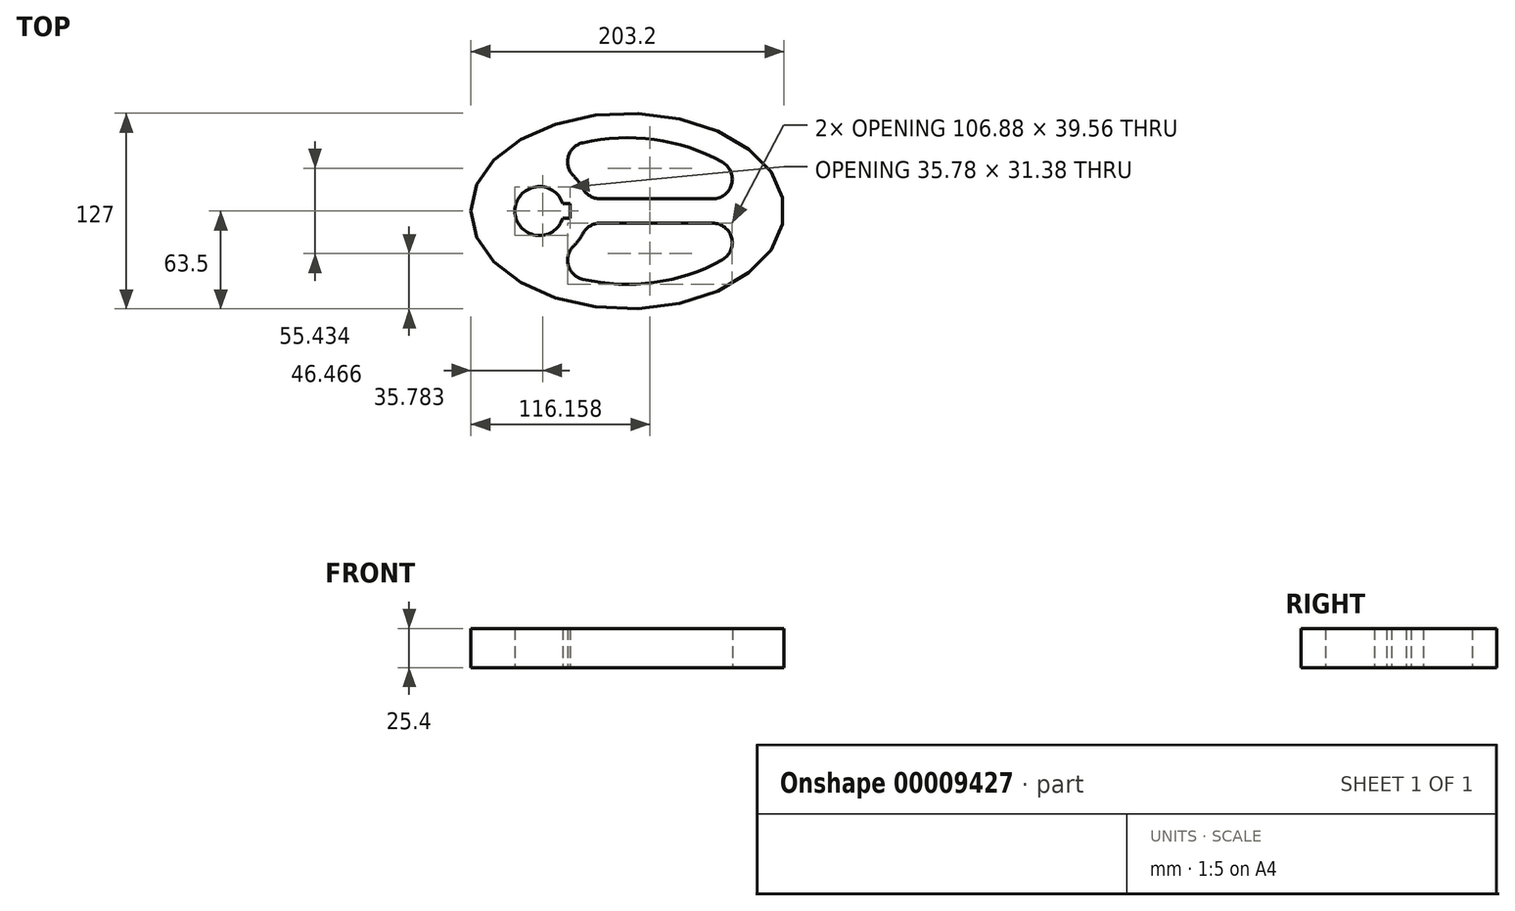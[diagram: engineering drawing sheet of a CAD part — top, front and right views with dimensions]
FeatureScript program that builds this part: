
annotation { "Feature Type Name" : "Feature", "Feature Type Description" : "" }
export const myFeature = defineFeature(function(context is Context, id is Id, definition is map)
    precondition{}
    {
        {
            var Q0;
            Q0=qCreatedBy(makeId("Top.planeOp"),FACE);
            var sketch = newSketch(context, id + "F0", { "sketchPlane" : qUnion([Q0])});
            skEllipse(sketch, "E0", {"center": v(0, 0) * mm, "majorRadius": 101.6 * mm, "minorRadius": 63.5 * mm, "majorAxis": v(-1, 0)});
            skCircle(sketch, "E1", {"center": v(-57.15, 0) * mm, "radius": 31.75 * mm});
            skArc(sketch, "E2", {"start": v(-42, 4.76) * mm, "mid": v(-73.03, 0) * mm, "end": v(-42, -4.76) * mm});
            skArc(sketch, "E3", {"start": v(-29.03, 14.74) * mm, "mid": v(-31.71, 19) * mm, "end": v(-35.03, 22.78) * mm});
            skLineSegment(sketch, "E4", {"start": v(-17.78, 7.94) * mm, "end": v(55.34, 7.94) * mm});
            skArc(sketch, "E5", {"start": v(-35.03, -22.78) * mm, "mid": v(-31.71, -19) * mm, "end": v(-29.03, -14.74) * mm});
            skLineSegment(sketch, "E6", {"start": v(-17.78, -7.94) * mm, "end": v(55.34, -7.94) * mm});
            skArc(sketch, "E7.filletArc", {"start": v(-29.03, 14.74) * mm, "mid": v(-24.35, 9.77) * mm, "end": v(-17.78, 7.94) * mm});
            skArc(sketch, "E8.filletArc", {"start": v(-17.78, -7.94) * mm, "mid": v(-24.35, -9.77) * mm, "end": v(-29.03, -14.74) * mm});
            skArc(sketch, "E9", {"start": v(61.48, 31.75) * mm, "mid": v(17.36, 46.43) * mm, "end": v(-29.1, 44.25) * mm});
            skArc(sketch, "E10", {"start": v(-29.1, 44.25) * mm, "mid": v(-38.42, 35.27) * mm, "end": v(-35.03, 22.78) * mm});
            skArc(sketch, "E11", {"start": v(55.34, 7.94) * mm, "mid": v(67.63, 17.46) * mm, "end": v(61.48, 31.75) * mm});
            skLineSegment(sketch, "E12", {"start": v(0, 63.5) * mm, "end": v(112.48, 63.5) * mm, "construction": true});
            skLineSegment(sketch, "E13", {"start": v(0, 47.62) * mm, "end": v(112.48, 47.62) * mm, "construction": true});
            skArc(sketch, "E14", {"start": v(-29.1, -44.25) * mm, "mid": v(17.36, -46.43) * mm, "end": v(61.48, -31.75) * mm});
            skArc(sketch, "E15", {"start": v(-35.03, -22.78) * mm, "mid": v(-38.42, -35.27) * mm, "end": v(-29.1, -44.25) * mm});
            skArc(sketch, "E16", {"start": v(55.34, -7.94) * mm, "mid": v(67.63, -17.46) * mm, "end": v(61.48, -31.75) * mm});
            skLineSegment(sketch, "E17", {"start": v(0, -47.62) * mm, "end": v(99.83, -47.62) * mm, "construction": true});
            skLineSegment(sketch, "E18", {"start": v(0, -63.5) * mm, "end": v(99.83, -63.5) * mm, "construction": true});
            skLineSegment(sketch, "E19", {"start": v(-42, 4.76) * mm, "end": v(-37.24, 4.76) * mm});
            skLineSegment(sketch, "E20", {"start": v(-37.24, 4.76) * mm, "end": v(-37.24, 0) * mm});
            skLineSegment(sketch, "E21.0.MirrorCS", {"start": v(-42, -4.76) * mm, "end": v(-37.24, -4.76) * mm});
            skLineSegment(sketch, "E21.1.MirrorCS", {"start": v(-37.24, -4.76) * mm, "end": v(-37.24, 0) * mm});
            skSolve(sketch);
        }
        {
            var Q0;
            Q0=makeQuery(id+"F0.imprint","IMPRINT",FACE,{"disambiguationData":[TD([[makeQuery(id+"F0.imprint","IMPRINT",EDGE,{"derivedFrom":sQuery(id+"F0.wireOp",EDGE,"E0")}),1.0]])]});
            var Q1;
            Q1=makeQuery(id+"F0.imprint","IMPRINT",FACE,{"disambiguationData":[TD([[makeQuery(id+"F0.imprint","IMPRINT",EDGE,{"derivedFrom":sQuery(id+"F0.wireOp",EDGE,"E2")}),-1.0]])]});
            extrude(context, id + "F1", {"entities" : qUnion([Q0, Q1]), "depth" : 25.4 * mm});
        }
    });
